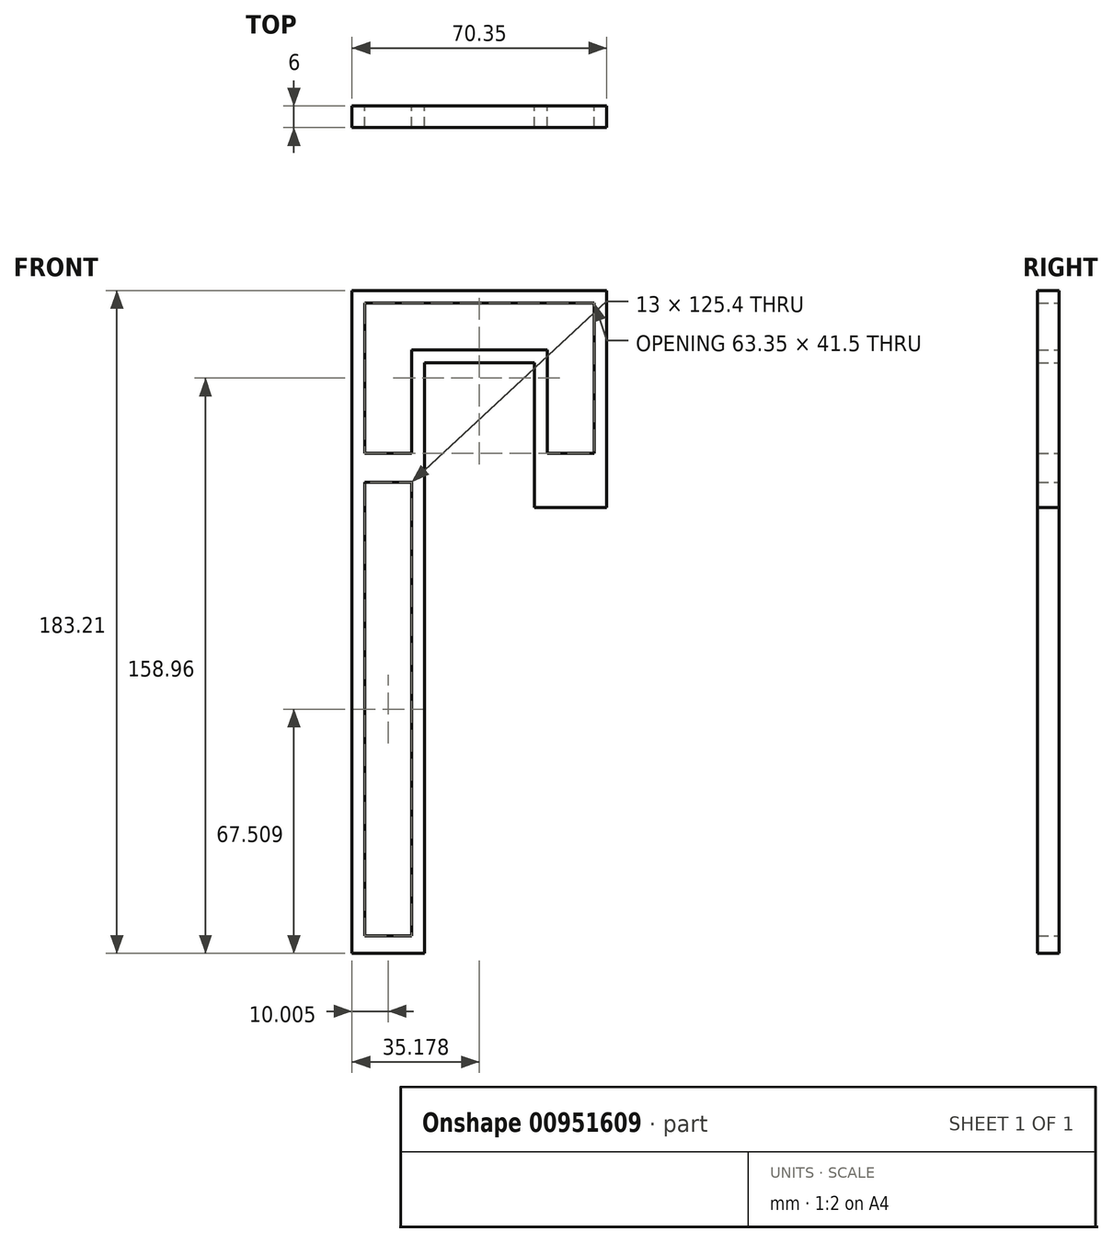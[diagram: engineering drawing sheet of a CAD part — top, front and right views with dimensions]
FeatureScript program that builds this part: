
annotation { "Feature Type Name" : "Feature", "Feature Type Description" : "" }
export const myFeature = defineFeature(function(context is Context, id is Id, definition is map)
    precondition{}
    {
        {
            var Q0;
            Q0=qCreatedBy(makeId("Front.planeOp"),FACE);
            var sketch = newSketch(context, id + "F0", { "sketchPlane" : qUnion([Q0])});
            skLineSegment(sketch, "E0.0.0", {"start": v(60.4, 90) * mm, "end": v(-9.96, 90) * mm});
            skLineSegment(sketch, "E0.0.1", {"start": v(-9.96, 90) * mm, "end": v(-9.96, -93.2) * mm});
            skLineSegment(sketch, "E0.0.2", {"start": v(-9.96, -93.2) * mm, "end": v(10.04, -93.2) * mm});
            skLineSegment(sketch, "E0.0.3", {"start": v(10.04, -93.2) * mm, "end": v(10.04, 70.06) * mm});
            skLineSegment(sketch, "E0.0.4", {"start": v(10.04, 70.06) * mm, "end": v(40.44, 70.06) * mm});
            skLineSegment(sketch, "E0.0.5", {"start": v(40.44, 70.06) * mm, "end": v(40.44, 30) * mm});
            skLineSegment(sketch, "E0.0.6", {"start": v(40.44, 30) * mm, "end": v(60.4, 30) * mm});
            skLineSegment(sketch, "E0.0.7", {"start": v(60.4, 30) * mm, "end": v(60.4, 90) * mm});
            skLineSegment(sketch, "E1", {"start": v(40.44, 41) * mm, "end": v(60.4, 41) * mm, "construction": true});
            skLineSegment(sketch, "E2.bottom", {"start": v(-6.46, -88.4) * mm, "end": v(6.54, -88.4) * mm});
            skLineSegment(sketch, "E3", {"start": v(-6.46, 45) * mm, "end": v(-6.46, 73.98) * mm});
            skLineSegment(sketch, "E4", {"start": v(56.9, 73.98) * mm, "end": v(56.9, 45) * mm});
            skLineSegment(sketch, "E5", {"start": v(56.9, 45) * mm, "end": v(43.94, 45) * mm});
            skLineSegment(sketch, "E6", {"start": v(43.94, 45) * mm, "end": v(43.94, 73.56) * mm});
            skLineSegment(sketch, "E7", {"start": v(43.94, 73.56) * mm, "end": v(6.54, 73.56) * mm});
            skLineSegment(sketch, "E8", {"start": v(6.54, 73.56) * mm, "end": v(6.54, 45) * mm});
            skLineSegment(sketch, "E9", {"start": v(6.54, 45) * mm, "end": v(-6.46, 45) * mm});
            skLineSegment(sketch, "E10", {"start": v(-6.46, 37) * mm, "end": v(6.54, 37) * mm});
            skLineSegment(sketch, "E11", {"start": v(6.54, 37) * mm, "end": v(6.54, -88.4) * mm});
            skLineSegment(sketch, "E12", {"start": v(-6.46, -88.4) * mm, "end": v(-6.46, 37) * mm});
            skLineSegment(sketch, "E13", {"start": v(40.44, 41) * mm, "end": v(-9.96, 41) * mm, "construction": true});
            skLineSegment(sketch, "E14", {"start": v(-6.46, 73.98) * mm, "end": v(-6.46, 86.5) * mm});
            skLineSegment(sketch, "E15", {"start": v(-6.46, 86.5) * mm, "end": v(56.9, 86.5) * mm});
            skLineSegment(sketch, "E16", {"start": v(56.9, 86.5) * mm, "end": v(56.9, 73.98) * mm});
            skSolve(sketch);
        }
        {
            var Q0;
            Q0=makeQuery(id+"F0.imprint","IMPRINT",FACE,{"disambiguationData":[TD([[makeQuery(id+"F0.imprint","IMPRINT",EDGE,{"derivedFrom":sQuery(id+"F0.wireOp",EDGE,"E0.0.0")}),1.0]])]});
            extrude(context, id + "F1", {"entities" : qUnion([Q0]), "depth" : 6 * mm, "offsetDistance" : 25 * mm});
        }
    });
